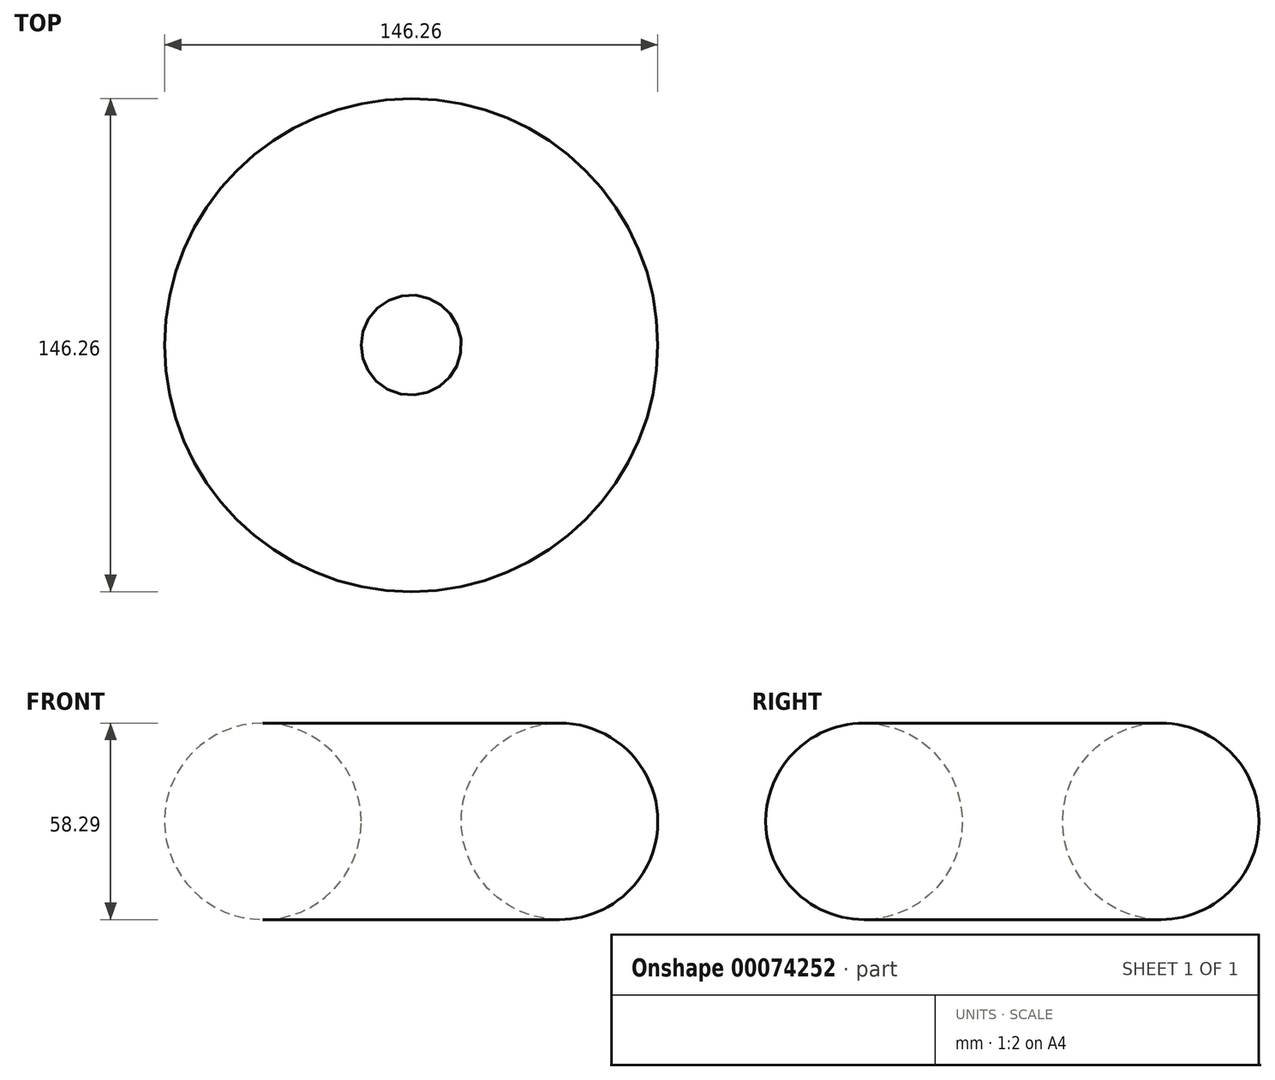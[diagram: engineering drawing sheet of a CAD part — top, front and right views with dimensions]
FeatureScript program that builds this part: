
annotation { "Feature Type Name" : "Feature", "Feature Type Description" : "" }
export const myFeature = defineFeature(function(context is Context, id is Id, definition is map)
    precondition{}
    {
        {
            var Q0;
            Q0=qCreatedBy(makeId("Front.planeOp"),FACE);
            var sketch = newSketch(context, id + "F0", { "sketchPlane" : qUnion([Q0])});
            skCircle(sketch, "E0", {"center": v(-43.98, 12.86) * mm, "radius": 29.14 * mm});
            skLineSegment(sketch, "E1", {"start": v(0, 0) * mm, "end": v(0, 94.6) * mm});
            skSolve(sketch);
        }
        {
            var Q0;
            Q0=makeQuery(id+"F0.imprint","IMPRINT",FACE,{"disambiguationData":[TD([[makeQuery(id+"F0.imprint","IMPRINT",EDGE,{"derivedFrom":sQuery(id+"F0.wireOp",EDGE,"E0")}),1.0]])]});
            var Q1;
            Q1=sQuery(id+"F0.wireOp",EDGE,"E1");
            revolve(context, id + "F1", {"entities" : qUnion([Q0]), "axis" : qUnion([Q1]), "revolveType" : RevolveType.FULL});
        }
    });
